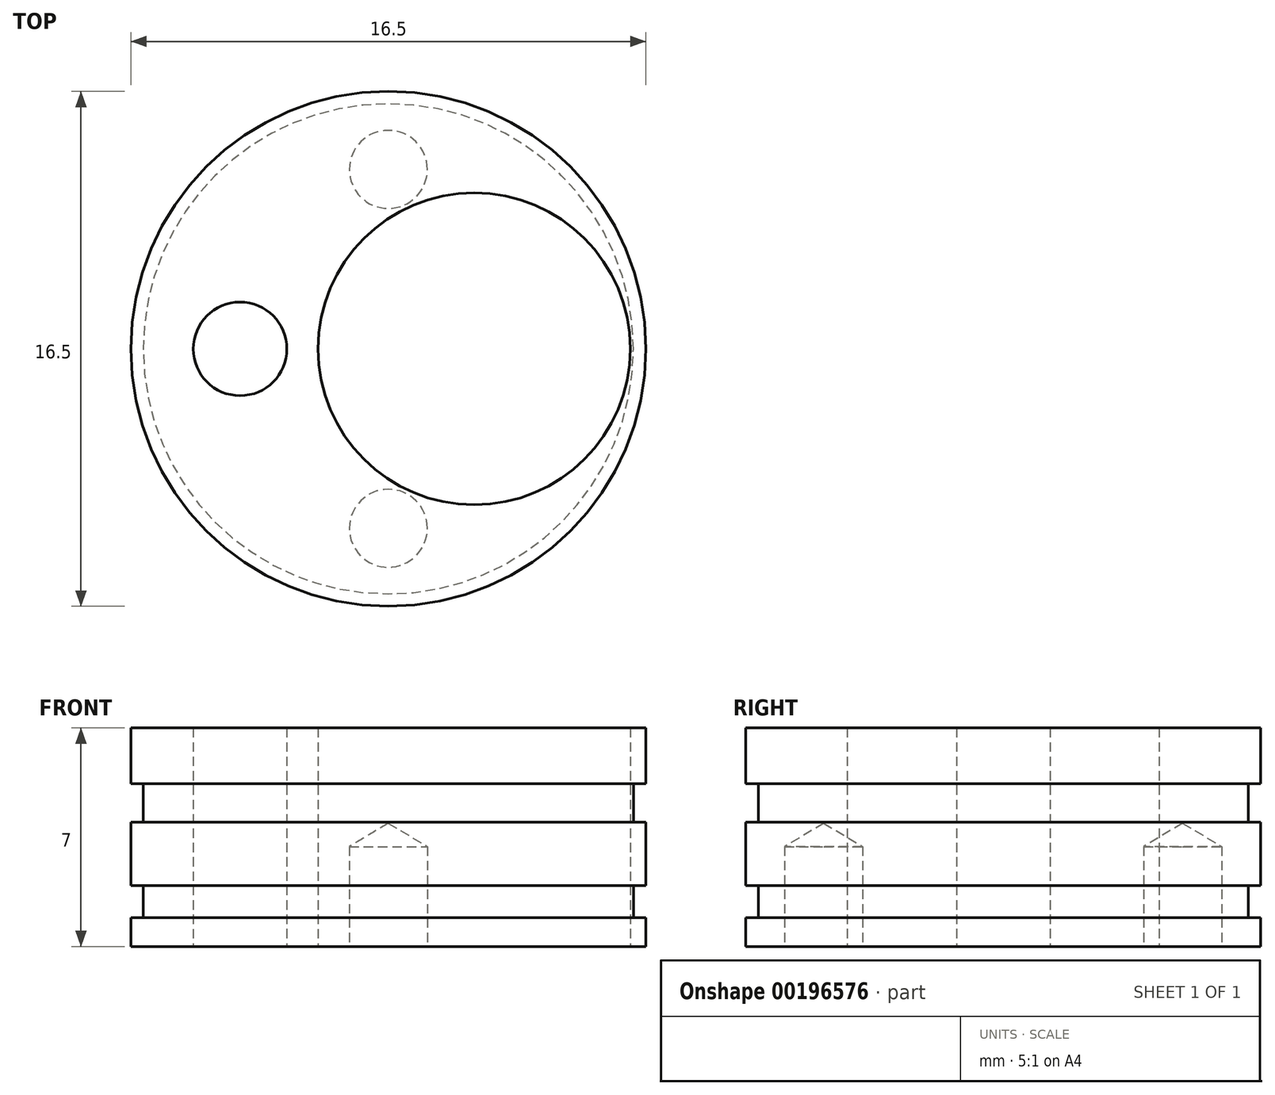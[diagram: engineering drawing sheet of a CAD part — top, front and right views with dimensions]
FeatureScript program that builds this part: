
annotation { "Feature Type Name" : "Feature", "Feature Type Description" : "" }
export const myFeature = defineFeature(function(context is Context, id is Id, definition is map)
    precondition{}
    {
        {
            var Q0;
            Q0=qCreatedBy(makeId("Front.planeOp"),FACE);
            var sketch = newSketch(context, id + "F0", { "sketchPlane" : qUnion([Q0])});
            skLineSegment(sketch, "E0", {"start": v(0, 7) * mm, "end": v(8.25, 7) * mm});
            skLineSegment(sketch, "E1", {"start": v(8.25, 7) * mm, "end": v(8.25, 5.22) * mm});
            skLineSegment(sketch, "E2", {"start": v(8.25, 5.22) * mm, "end": v(7.85, 5.22) * mm});
            skLineSegment(sketch, "E3", {"start": v(7.85, 5.22) * mm, "end": v(7.85, 3.98) * mm});
            skLineSegment(sketch, "E4", {"start": v(7.85, 3.98) * mm, "end": v(8.25, 3.98) * mm});
            skLineSegment(sketch, "E5", {"start": v(8.25, 3.98) * mm, "end": v(8.25, 1.94) * mm});
            skLineSegment(sketch, "E6", {"start": v(8.25, 1.94) * mm, "end": v(7.85, 1.94) * mm});
            skLineSegment(sketch, "E7", {"start": v(7.85, 1.94) * mm, "end": v(7.85, 0.92) * mm});
            skLineSegment(sketch, "E8", {"start": v(7.85, 0.92) * mm, "end": v(8.25, 0.92) * mm});
            skLineSegment(sketch, "E9", {"start": v(8.25, 0.92) * mm, "end": v(8.25, 0) * mm});
            skLineSegment(sketch, "E10", {"start": v(8.25, 0) * mm, "end": v(0, 0) * mm});
            skLineSegment(sketch, "E11", {"start": v(0, 0) * mm, "end": v(0, 7) * mm});
            skSolve(sketch);
        }
        {
            var Q0;
            Q0 = qSketchRegion(id + "F0", true);
            var Q1;
            Q1=sQuery(id+"F0.wireOp",EDGE,"E11");
            revolve(context, id + "F1", {"entities" : qUnion([Q0]), "axis" : qUnion([Q1]), "revolveType" : RevolveType.FULL});
        }
        {
            var Q0;
            Q0=qCreatedBy(makeId("Top.planeOp"),FACE);
            var sketch = newSketch(context, id + "F2", { "sketchPlane" : qUnion([Q0])});
            skCircle(sketch, "E12", {"center": v(2.75, 0) * mm, "radius": 5 * mm});
            skCircle(sketch, "E13", {"center": v(0, 5.75) * mm, "radius": 1.2 * mm});
            skLineSegment(sketch, "E14", {"start": v(-8.89, 0) * mm, "end": v(9, 0) * mm, "construction": true});
            skCircle(sketch, "E15.MirrorC", {"center": v(0, -5.75) * mm, "radius": 1.2 * mm});
            skCircle(sketch, "E16", {"center": v(-4.75, 0) * mm, "radius": 1.5 * mm});
            skSolve(sketch);
        }
        {
            var Q0;
            Q0=makeQuery(id+"F2.imprint","IMPRINT",FACE,{"disambiguationData":[TD([[makeQuery(id+"F2.imprint","IMPRINT",EDGE,{"derivedFrom":sQuery(id+"F2.wireOp",EDGE,"E12")}),1.0]])]});
            var Q1;
            Q1=makeQuery(id+"F2.imprint","IMPRINT",FACE,{"disambiguationData":[TD([[makeQuery(id+"F2.imprint","IMPRINT",EDGE,{"derivedFrom":sQuery(id+"F2.wireOp",EDGE,"E16")}),1.0]])]});
            var Q2;
            Q2=makeQuery(id+"F1.opRevolve","SWEPT_FACE",FACE,{"disambiguationData":[OSD([sQuery(id+"F0.wireOp",EDGE,"E0")])]});
            extrude(context, id + "F3", {"entities" : qUnion([Q0, Q1]), "operationType" : NewBodyOperationType.REMOVE, "endBound" : BoundingType.THROUGH_ALL, "endBoundEntityFace" : qUnion([Q2]), "depth" : 20 * mm});
        }
        {
            var Q0;
            Q0=sQuery(id+"F2.wireOp",VERTEX,"E15.MirrorC.center");
            var Q1;
            Q1=sQuery(id+"F2.wireOp",VERTEX,"E13.center");
            var Q2;
            Q2=makeQuery(id+"F1.opRevolve","SWEPT_BODY",BODY,{"disambiguationData":[OSD([sQuery(id+"F0.wireOp",EDGE,"E0"),sQuery(id+"F0.wireOp",EDGE,"E1"),sQuery(id+"F0.wireOp",EDGE,"E2"),sQuery(id+"F0.wireOp",EDGE,"E3"),sQuery(id+"F0.wireOp",EDGE,"E4"),sQuery(id+"F0.wireOp",EDGE,"E5"),sQuery(id+"F0.wireOp",EDGE,"E6"),sQuery(id+"F0.wireOp",EDGE,"E7"),sQuery(id+"F0.wireOp",EDGE,"E8"),sQuery(id+"F0.wireOp",EDGE,"E9"),sQuery(id+"F0.wireOp",EDGE,"E10"),sQuery(id+"F0.wireOp",EDGE,"E11")])]});
            hole(context, id + "F4", {"style" : HoleStyle.SIMPLE, "endStyle" : HoleEndStyle.BLIND, "oppositeDirection" : true, "holeDiameter" : 2.5 * mm, "holeDepth" : 3.2 * mm, "locations" : qUnion([Q0, Q1]), "scope" : qUnion([Q2])});
        }
        {
            var Q0;
            Q0=makeQuery(id+"F2.imprint","IMPRINT",FACE,{"disambiguationData":[TD([[makeQuery(id+"F2.imprint","IMPRINT",EDGE,{"derivedFrom":sQuery(id+"F2.wireOp",EDGE,"E13")}),1.0]])]});
            var Q1;
            Q1=makeQuery(id+"F2.imprint","IMPRINT",FACE,{"disambiguationData":[TD([[makeQuery(id+"F2.imprint","IMPRINT",EDGE,{"derivedFrom":sQuery(id+"F2.wireOp",EDGE,"E15.MirrorC")}),-1.0]])]});
            extrude(context, id + "F5", {"entities" : qUnion([Q0, Q1]), "operationType" : NewBodyOperationType.REMOVE, "depth" : 3.2 * mm});
        }
    });
